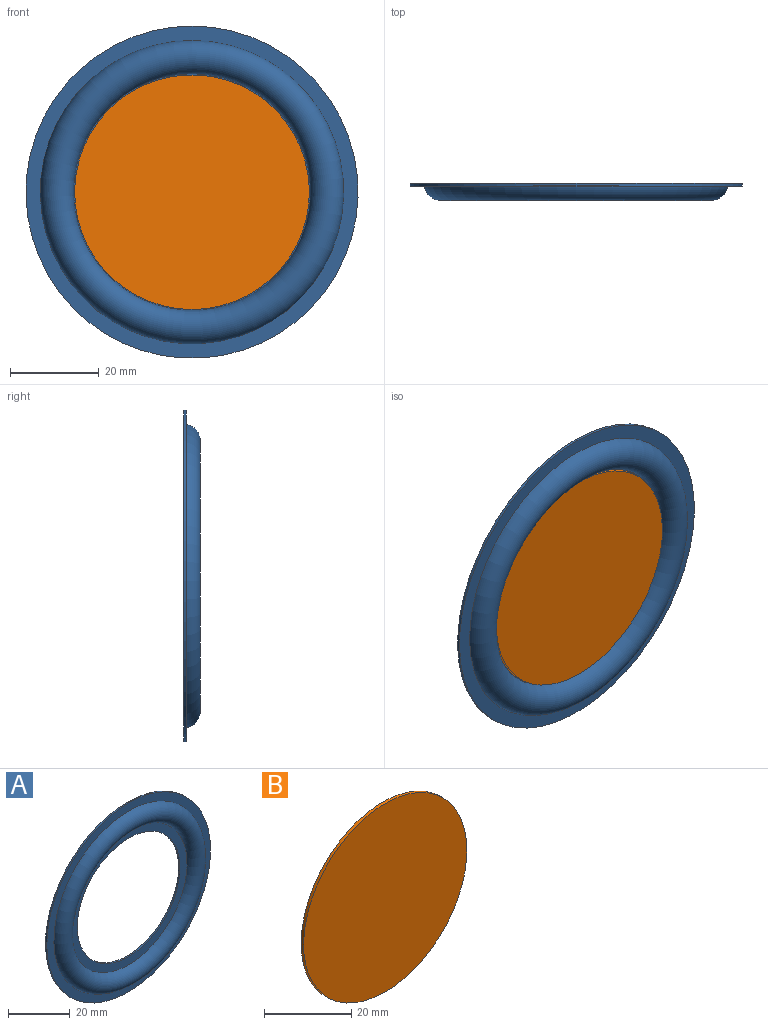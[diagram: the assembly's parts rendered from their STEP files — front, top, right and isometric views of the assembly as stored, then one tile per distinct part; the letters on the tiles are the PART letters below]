
ASSEMBLY  parts=2 mates=1
PART A: 8 faces, bbox 75x6.1x75 mm
  f0: cylinder r=23.5mm len=47mm, axis (0,1,0), area 88.6mm2, adj f1,f7
  f1: plane 53.5x53.5mm, normal (0,-1,0), area 512.7mm2, adj f0,f2
  f2: torus R=30.5mm, axis (0,1,0), area 2056.8mm2, adj f1,f3
  f3: plane 75x75mm, normal (0,-1,0), area 732.1mm2, adj f2,f4
  f4: cylinder r=37.5mm len=75mm, axis (0,1,0), area 141.4mm2, adj f3,f5
  f5: plane 75x75mm, normal (0,1,0), area 850mm2, adj f4,f6
  f6: torus R=30.5mm, axis (0,1,0), area 1926.5mm2, adj f5,f7
  f7: plane 54.6x54.6mm, normal (0,1,0), area 606.5mm2, adj f0,f6
PART B: 3 faces, bbox 53x0.8x53 mm
  f0: cylinder r=26.5mm len=53mm, axis (0,1,0), area 133.2mm2, adj f1,f2
  f1: plane 53x53mm, normal (0,-1,0), area 2206.2mm2, adj f0
  f2: plane 53x53mm, normal (0,1,0), area 2206.2mm2, adj f0
PLACE A t=(42,-6.1,0)mm
PLACE B t=(42,-6.1,0)mm
MATE fastened B.f0 <-> A.f0  axis (0,1,0) through (42,-6.1,0)mm
